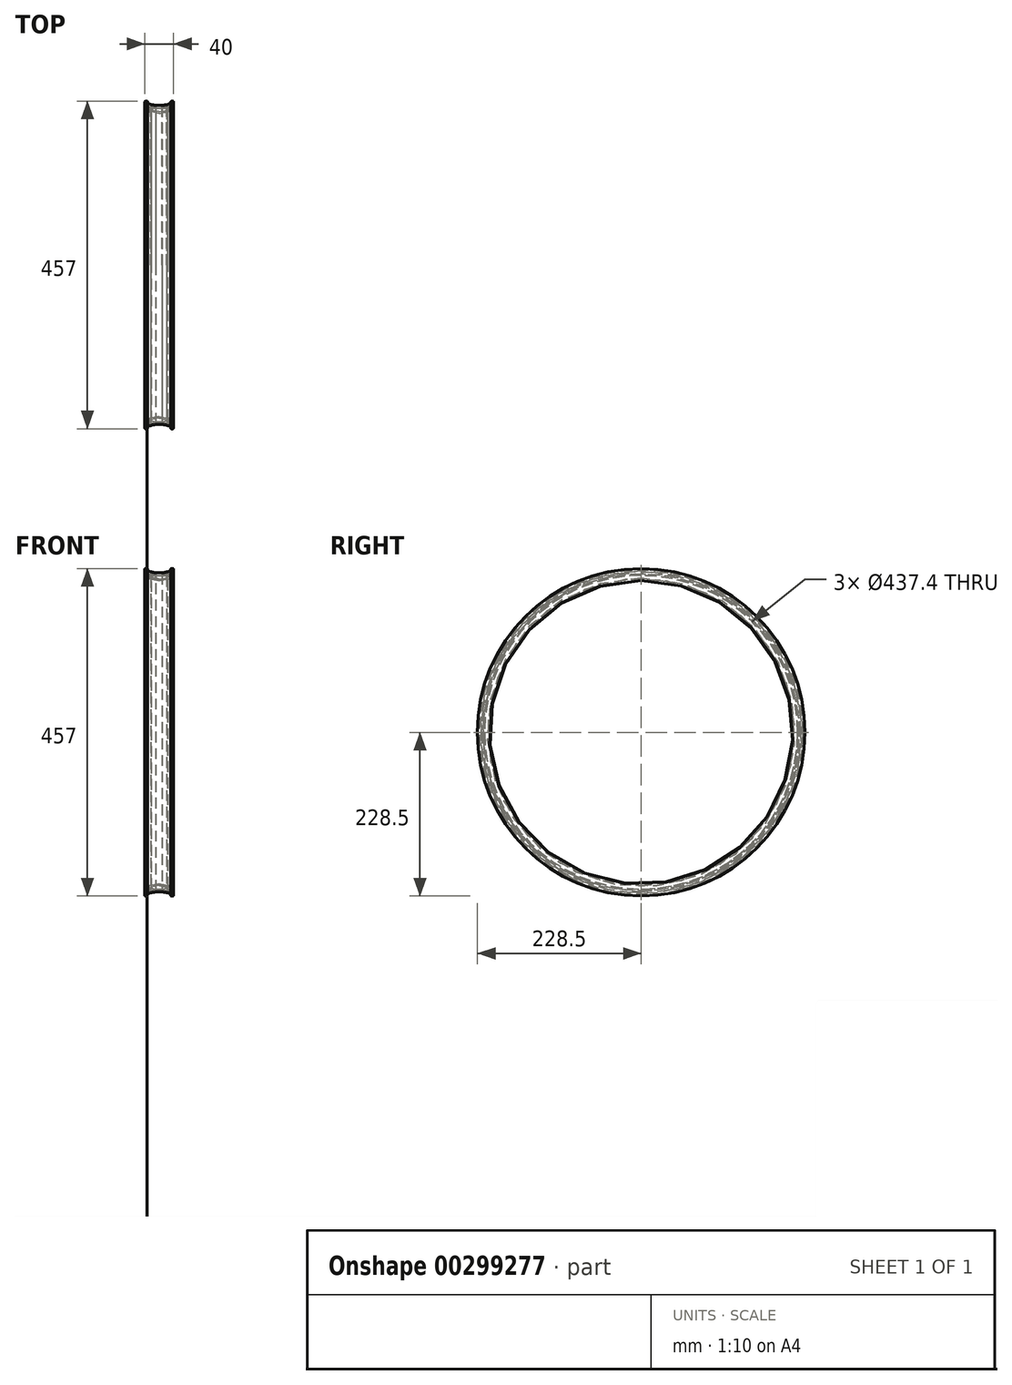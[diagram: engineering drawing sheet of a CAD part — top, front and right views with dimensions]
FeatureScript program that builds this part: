
annotation { "Feature Type Name" : "Feature", "Feature Type Description" : "" }
export const myFeature = defineFeature(function(context is Context, id is Id, definition is map)
    precondition{}
    {
        {
            var Q0;
            Q0=qCreatedBy(makeId("Front.planeOp"),FACE);
            var sketch = newSketch(context, id + "F0", { "sketchPlane" : qUnion([Q0])});
            skLineSegment(sketch, "E0", {"start": v(-20, 0) * mm, "end": v(-20, 17) * mm});
            skPoint(sketch, "E1", {"position": v(-17, 0) * mm});
            skPoint(sketch, "E2", {"position": v(-20, 2.5) * mm});
            skPoint(sketch, "E3", {"position": v(-18, 2.5) * mm});
            skPoint(sketch, "E4", {"position": v(-17, 2.5) * mm});
            skArc(sketch, "E5", {"start": v(-17, 0) * mm, "mid": v(-16.14, 1.25) * mm, "end": v(-17, 2.5) * mm});
            skLineSegment(sketch, "E6", {"start": v(0, 0) * mm, "end": v(0, 228.5) * mm, "construction": true});
            skPoint(sketch, "E7", {"position": v(-18, 3.3) * mm});
            skPoint(sketch, "E8", {"position": v(-18, 7.8) * mm});
            skPoint(sketch, "E9", {"position": v(0, 7.8) * mm});
            skPoint(sketch, "E10", {"position": v(-1, 7.8) * mm});
            skLineSegment(sketch, "E11", {"start": v(-18, 3.3) * mm, "end": v(-1, 7.8) * mm});
            skLineSegment(sketch, "E12", {"start": v(-18, 7.8) * mm, "end": v(-1, 7.8) * mm});
            skLineSegment(sketch, "E13", {"start": v(-18, 7.8) * mm, "end": v(-18, 3.3) * mm});
            skPoint(sketch, "E14", {"position": v(-18, 9.8) * mm});
            skLineSegment(sketch, "E15", {"start": v(-20, 17) * mm, "end": v(-13.56, 14.26) * mm});
            skLineSegment(sketch, "E16", {"start": v(-18, 9.8) * mm, "end": v(-18, 13.8) * mm});
            skLineSegment(sketch, "E17", {"start": v(-18, 13.8) * mm, "end": v(-15.33, 12.67) * mm});
            skLineSegment(sketch, "E18", {"start": v(-18, 13.8) * mm, "end": v(-8.58, 9.8) * mm});
            skLineSegment(sketch, "E19", {"start": v(-18, 9.8) * mm, "end": v(-8.58, 9.8) * mm});
            skLineSegment(sketch, "E20", {"start": v(-13.56, 14.26) * mm, "end": v(0, 17) * mm});
            skLineSegment(sketch, "E21", {"start": v(-20, 0) * mm, "end": v(-17, 0) * mm});
            skLineSegment(sketch, "E22", {"start": v(0, 14.96) * mm, "end": v(-13.23, 12.29) * mm});
            skLineSegment(sketch, "E23", {"start": v(-13.23, 12.29) * mm, "end": v(-7.37, 9.8) * mm});
            skLineSegment(sketch, "E24", {"start": v(-7.37, 9.8) * mm, "end": v(0, 9.8) * mm});
            skLineSegment(sketch, "E25.MirrorCS", {"start": v(0, 14.96) * mm, "end": v(13.23, 12.29) * mm});
            skLineSegment(sketch, "E26.MirrorCS", {"start": v(13.56, 14.26) * mm, "end": v(0, 17) * mm});
            skLineSegment(sketch, "E27.MirrorCS", {"start": v(20, 17) * mm, "end": v(13.56, 14.26) * mm});
            skLineSegment(sketch, "E28.MirrorCS", {"start": v(20, 0) * mm, "end": v(20, 17) * mm});
            skLineSegment(sketch, "E29.MirrorCS", {"start": v(18, 13.8) * mm, "end": v(8.58, 9.8) * mm});
            skLineSegment(sketch, "E30.MirrorCS", {"start": v(18, 9.8) * mm, "end": v(18, 13.8) * mm});
            skLineSegment(sketch, "E31.MirrorCS", {"start": v(18, 9.8) * mm, "end": v(8.58, 9.8) * mm});
            skLineSegment(sketch, "E32.MirrorCS", {"start": v(13.23, 12.29) * mm, "end": v(7.37, 9.8) * mm});
            skLineSegment(sketch, "E33.MirrorCS", {"start": v(7.37, 9.8) * mm, "end": v(0, 9.8) * mm});
            skLineSegment(sketch, "E34.MirrorCS", {"start": v(18, 7.8) * mm, "end": v(1, 7.8) * mm});
            skLineSegment(sketch, "E35.MirrorCS", {"start": v(18, 3.3) * mm, "end": v(1, 7.8) * mm});
            skArc(sketch, "E36.MirrorCS", {"start": v(17, 0) * mm, "mid": v(16.14, 1.25) * mm, "end": v(17, 2.5) * mm});
            skLineSegment(sketch, "E37.MirrorCS", {"start": v(20, 0) * mm, "end": v(17, 0) * mm});
            skLineSegment(sketch, "E38", {"start": v(-18, 2.5) * mm, "end": v(-17, 2.5) * mm});
            skLineSegment(sketch, "E39", {"start": v(18, 3.3) * mm, "end": v(18, 7.8) * mm});
            skPoint(sketch, "E40.endSnap0", {"position": v(18, 5.55) * mm});
            skLineSegment(sketch, "E41", {"start": v(17, 2.5) * mm, "end": v(18, 2.5) * mm});
            skArc(sketch, "E42", {"start": v(18, 2.5) * mm, "mid": v(0, 6.07) * mm, "end": v(-18, 2.5) * mm});
            skLineSegment(sketch, "E43", {"start": v(0, 228.5) * mm, "end": v(-69.94, 228.5) * mm, "construction": true});
            skPoint(sketch, "E44", {"position": v(0, 6.07) * mm});
            skPoint(sketch, "E45", {"position": v(0, 14.26) * mm});
            skSolve(sketch);
        }
        {
            var Q0;
            Q0=makeQuery(id+"F0.imprint","IMPRINT",FACE,{"disambiguationData":[TD([[makeQuery(id+"F0.imprint","IMPRINT",EDGE,{"derivedFrom":sQuery(id+"F0.wireOp",EDGE,"E0")}),-1.0]])]});
            var Q1;
            Q1=sQuery(id+"F0.wireOp",EDGE,"E43");
            revolve(context, id + "F1", {"entities" : qUnion([Q0]), "axis" : qUnion([Q1]), "revolveType" : RevolveType.TWO_DIRECTIONS, "angle" : 360 * degree, "angleBack" : 0 * degree});
        }
        {
            var Q0;
            Q0=makeQuery(id+"F1.opRevolve","SWEPT_EDGE",EDGE,{"disambiguationData":[OSD([sQuery(id+"F0.wireOp",EDGE,"E26.MirrorCS"),sQuery(id+"F0.wireOp",EDGE,"E27.MirrorCS")])]});
            var Q1;
            Q1=makeQuery(id+"F1.opRevolve","SWEPT_EDGE",EDGE,{"disambiguationData":[OSD([sQuery(id+"F0.wireOp",EDGE,"E15"),sQuery(id+"F0.wireOp",EDGE,"E20")])]});
            fillet(context, id + "F2", {"entities" : qUnion([Q0, Q1]), "radius" : 1 * mm, "tangentPropagation" : true, "allowEdgeOverflow" : false});
        }
        {
            var Q0;
            Q0=makeQuery(id+"F1.opRevolve","SWEPT_EDGE",EDGE,{"disambiguationData":[OSD([sQuery(id+"F0.wireOp",EDGE,"E0"),sQuery(id+"F0.wireOp",EDGE,"E15")])]});
            var Q1;
            Q1=makeQuery(id+"F1.opRevolve","SWEPT_EDGE",EDGE,{"disambiguationData":[OSD([sQuery(id+"F0.wireOp",EDGE,"E27.MirrorCS"),sQuery(id+"F0.wireOp",EDGE,"E28.MirrorCS")])]});
            var Q2;
            Q2=makeQuery(id+"F1.opRevolve","SWEPT_EDGE",EDGE,{"disambiguationData":[OSD([sQuery(id+"F0.wireOp",EDGE,"E28.MirrorCS"),sQuery(id+"F0.wireOp",EDGE,"E37.MirrorCS")])]});
            var Q3;
            Q3=makeQuery(id+"F1.opRevolve","SWEPT_EDGE",EDGE,{"disambiguationData":[OSD([sQuery(id+"F0.wireOp",EDGE,"E0"),sQuery(id+"F0.wireOp",EDGE,"E21")])]});
            fillet(context, id + "F3", {"entities" : qUnion([Q0, Q1, Q2, Q3]), "radius" : 1 * mm, "tangentPropagation" : true, "allowEdgeOverflow" : false});
        }
        {
            var Q0;
            Q0=makeQuery(id+"F1.opRevolve","SWEPT_EDGE",EDGE,{"disambiguationData":[OSD([sQuery(id+"F0.wireOp",EDGE,"E32.MirrorCS"),sQuery(id+"F0.wireOp",EDGE,"E33.MirrorCS")])]});
            var Q1;
            Q1=makeQuery(id+"F1.opRevolve","SWEPT_EDGE",EDGE,{"disambiguationData":[OSD([sQuery(id+"F0.wireOp",EDGE,"E23"),sQuery(id+"F0.wireOp",EDGE,"E24")])]});
            var Q2;
            Q2=makeQuery(id+"F1.opRevolve","SWEPT_EDGE",EDGE,{"disambiguationData":[OSD([sQuery(id+"F0.wireOp",EDGE,"E22"),sQuery(id+"F0.wireOp",EDGE,"E25.MirrorCS")])]});
            var Q3;
            Q3=makeQuery(id+"F1.opRevolve","SWEPT_EDGE",EDGE,{"disambiguationData":[OSD([sQuery(id+"F0.wireOp",EDGE,"E22"),sQuery(id+"F0.wireOp",EDGE,"E23")])]});
            var Q4;
            Q4=makeQuery(id+"F1.opRevolve","SWEPT_EDGE",EDGE,{"disambiguationData":[OSD([sQuery(id+"F0.wireOp",EDGE,"E25.MirrorCS"),sQuery(id+"F0.wireOp",EDGE,"E32.MirrorCS")])]});
            fillet(context, id + "F4", {"entities" : qUnion([Q0, Q1, Q2, Q3, Q4]), "radius" : .5 * mm, "tangentPropagation" : true, "allowEdgeOverflow" : false});
        }
        {
            var Q0;
            Q0=makeQuery(id+"F1.opRevolve","SWEPT_EDGE",EDGE,{"disambiguationData":[OSD([sQuery(id+"F0.wireOp",EDGE,"E29.MirrorCS"),sQuery(id+"F0.wireOp",EDGE,"E30.MirrorCS")])]});
            var Q1;
            Q1=makeQuery(id+"F1.opRevolve","SWEPT_EDGE",EDGE,{"disambiguationData":[OSD([sQuery(id+"F0.wireOp",EDGE,"E30.MirrorCS"),sQuery(id+"F0.wireOp",EDGE,"E31.MirrorCS")])]});
            var Q2;
            Q2=makeQuery(id+"F1.opRevolve","SWEPT_EDGE",EDGE,{"disambiguationData":[OSD([sQuery(id+"F0.wireOp",EDGE,"E29.MirrorCS"),sQuery(id+"F0.wireOp",EDGE,"E31.MirrorCS")])]});
            var Q3;
            Q3=makeQuery(id+"F1.opRevolve","SWEPT_EDGE",EDGE,{"disambiguationData":[OSD([sQuery(id+"F0.wireOp",EDGE,"E16"),sQuery(id+"F0.wireOp",EDGE,"E18")])]});
            var Q4;
            Q4=makeQuery(id+"F1.opRevolve","SWEPT_EDGE",EDGE,{"disambiguationData":[OSD([sQuery(id+"F0.wireOp",EDGE,"E16"),sQuery(id+"F0.wireOp",EDGE,"E19")])]});
            var Q5;
            Q5=makeQuery(id+"F1.opRevolve","SWEPT_EDGE",EDGE,{"disambiguationData":[OSD([sQuery(id+"F0.wireOp",EDGE,"E18"),sQuery(id+"F0.wireOp",EDGE,"E19")])]});
            fillet(context, id + "F5", {"entities" : qUnion([Q0, Q1, Q2, Q3, Q4, Q5]), "radius" : .5 * mm, "tangentPropagation" : true, "allowEdgeOverflow" : false});
        }
        {
            var Q0;
            Q0=makeQuery(id+"F1.opRevolve","SWEPT_EDGE",EDGE,{"disambiguationData":[OSD([sQuery(id+"F0.wireOp",EDGE,"E35.MirrorCS"),sQuery(id+"F0.wireOp",EDGE,"E39")])]});
            var Q1;
            Q1=makeQuery(id+"F1.opRevolve","SWEPT_EDGE",EDGE,{"disambiguationData":[OSD([sQuery(id+"F0.wireOp",EDGE,"E34.MirrorCS"),sQuery(id+"F0.wireOp",EDGE,"E39")])]});
            var Q2;
            Q2=makeQuery(id+"F1.opRevolve","SWEPT_EDGE",EDGE,{"disambiguationData":[OSD([sQuery(id+"F0.wireOp",EDGE,"E34.MirrorCS"),sQuery(id+"F0.wireOp",EDGE,"E35.MirrorCS")])]});
            var Q3;
            Q3=makeQuery(id+"F1.opRevolve","SWEPT_EDGE",EDGE,{"disambiguationData":[OSD([sQuery(id+"F0.wireOp",EDGE,"E11"),sQuery(id+"F0.wireOp",EDGE,"E12")])]});
            var Q4;
            Q4=makeQuery(id+"F1.opRevolve","SWEPT_EDGE",EDGE,{"disambiguationData":[OSD([sQuery(id+"F0.wireOp",EDGE,"E11"),sQuery(id+"F0.wireOp",EDGE,"E13")])]});
            var Q5;
            Q5=makeQuery(id+"F1.opRevolve","SWEPT_EDGE",EDGE,{"disambiguationData":[OSD([sQuery(id+"F0.wireOp",EDGE,"E12"),sQuery(id+"F0.wireOp",EDGE,"E13")])]});
            fillet(context, id + "F6", {"entities" : qUnion([Q0, Q1, Q2, Q3, Q4, Q5]), "radius" : .5 * mm, "tangentPropagation" : true, "allowEdgeOverflow" : false});
        }
        {
            var Q0;
            Q0=makeQuery(id+"F1.opRevolve","SWEPT_EDGE",EDGE,{"disambiguationData":[OSD([sQuery(id+"F0.wireOp",EDGE,"E41"),sQuery(id+"F0.wireOp",EDGE,"E42")])]});
            var Q1;
            Q1=makeQuery(id+"F1.opRevolve","SWEPT_EDGE",EDGE,{"disambiguationData":[OSD([sQuery(id+"F0.wireOp",EDGE,"E38"),sQuery(id+"F0.wireOp",EDGE,"E42")])]});
            fillet(context, id + "F7", {"entities" : qUnion([Q0, Q1]), "radius" : .5 * mm, "tangentPropagation" : true, "allowEdgeOverflow" : false});
        }
        {
            var Q0;
            Q0=makeQuery(id+"F1.opRevolve","SWEPT_EDGE",EDGE,{"disambiguationData":[OSD([sQuery(id+"F0.wireOp",EDGE,"E20"),sQuery(id+"F0.wireOp",EDGE,"E26.MirrorCS")])]});
            fillet(context, id + "F8", {"entities" : qUnion([Q0]), "radius" : 1 * mm, "tangentPropagation" : true, "allowEdgeOverflow" : false});
        }
    });
